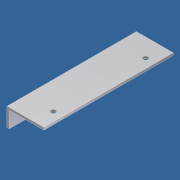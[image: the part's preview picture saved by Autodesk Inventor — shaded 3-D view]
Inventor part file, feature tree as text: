
AUTODESK INVENTOR PART (.ipt)
format: ipt  version: 2012 (Build 160160000, 160)  size: 79,872 bytes
history: native  units: in
note: dims shown in document units (in); Inventor stores cm internally (conversion verified against a paired STEP export)
features: extrude x1, hole x1, pattern_linear x1, sketch x1
ambient origin geometry x8: Origin, YZ Plane, XZ Plane, XY Plane, X Axis, Y Axis, Z Axis, Center Point
bodies: Solid1 (feature_tree)
feature tree (4):
  extrude  "Extrusion1"  Depth=2.0in
  hole  "Hole1"  [1 undecoded]
  pattern_linear  "Rectangular Pattern1"  Spacing1=7.0in  [1 undecoded]
  sketch  "Sketch1"  dims[d0=0.125in d1=2.0in d2=1.0in d3=7.0in d4=0.0in d5=1.0in d6=1.5in d7=0.265in d8=0.75in d9=0.375in d10=0.25in d11=0.5635in d12=1.0in d13=0.8108in d14=0.7874in d16=5.0in]
note: 2 required parameter values undecoded (feature->parameter linkage not recoverable at this tier; creation-order binding heuristic only, values carry confidence <= 0.55)
